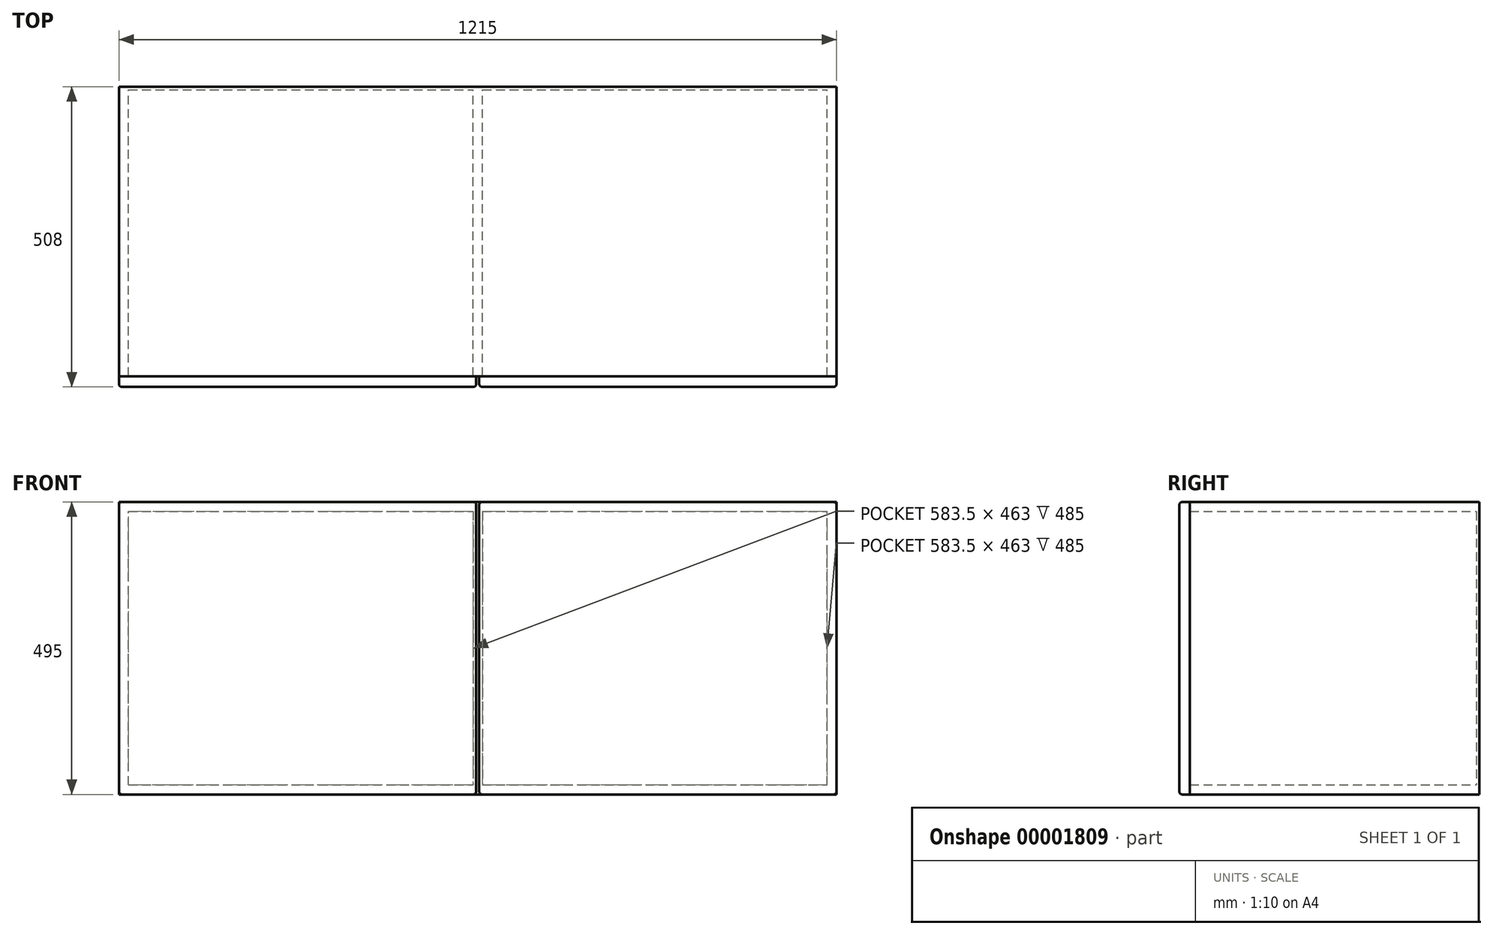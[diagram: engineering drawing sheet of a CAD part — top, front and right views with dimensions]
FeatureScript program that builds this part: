
annotation { "Feature Type Name" : "Feature", "Feature Type Description" : "" }
export const myFeature = defineFeature(function(context is Context, id is Id, definition is map)
    precondition{}
    {
        {
            var Q0;
            Q0=qCreatedBy(makeId("Front.planeOp"),FACE);
            var sketch = newSketch(context, id + "F0", { "sketchPlane" : qUnion([Q0])});
            skLineSegment(sketch, "E0.bottom", {"start": v(0, 0) * mm, "end": v(1215, 0) * mm});
            skLineSegment(sketch, "E0.top", {"start": v(0, 495) * mm, "end": v(1215, 495) * mm});
            skLineSegment(sketch, "E0.left", {"start": v(0, 0) * mm, "end": v(0, 495) * mm});
            skLineSegment(sketch, "E0.right", {"start": v(1215, 0) * mm, "end": v(1215, 495) * mm});
            skLineSegment(sketch, "E1.0", {"start": v(16, 16) * mm, "end": v(16, 479) * mm});
            skLineSegment(sketch, "E1.1", {"start": v(16, 16) * mm, "end": v(1199, 16) * mm});
            skLineSegment(sketch, "E1.2", {"start": v(1199, 16) * mm, "end": v(1199, 479) * mm});
            skLineSegment(sketch, "E1.3", {"start": v(16, 479) * mm, "end": v(1199, 479) * mm});
            skLineSegment(sketch, "E2", {"start": v(607.5, 479) * mm, "end": v(607.5, 16) * mm, "construction": true});
            skLineSegment(sketch, "E3.0", {"start": v(599.5, 479) * mm, "end": v(599.5, 16) * mm});
            skLineSegment(sketch, "E4.0", {"start": v(615.5, 479) * mm, "end": v(615.5, 16) * mm});
            skSolve(sketch);
        }
        {
            var Q0;
            Q0=makeQuery(id+"F0.imprint","IMPRINT",FACE,{"disambiguationData":[TD([[makeQuery(id+"F0.imprint","IMPRINT",EDGE,{"derivedFrom":sQuery(id+"F0.wireOp",EDGE,"E0.bottom")}),1.0]])]});
            var Q1;
            {var subQ1=sQuery(id+"F0.wireOp",EDGE,"E3.0");Q1=makeQuery(id+"F0.imprint","IMPRINT",FACE,{"disambiguationData":[TD([[makeQuery(id+"F0.imprint","IMPRINT",EDGE,{"derivedFrom":subQ1}),1.0]])]});}
            extrude(context, id + "F1", {"entities" : qUnion([Q0, Q1]), "depth" : 490 * mm});
        }
        {
            var Q0;
            {var subQ2=sQuery(id+"F0.wireOp",EDGE,"E1.0");Q0=makeQuery(id+"F0.imprint","IMPRINT",FACE,{"disambiguationData":[TD([[makeQuery(id+"F0.imprint","IMPRINT",EDGE,{"derivedFrom":subQ2}),-1.0]])]});}
            var Q1;
            {var subQ2=sQuery(id+"F0.wireOp",EDGE,"E1.2");Q1=makeQuery(id+"F0.imprint","IMPRINT",FACE,{"disambiguationData":[TD([[makeQuery(id+"F0.imprint","IMPRINT",EDGE,{"derivedFrom":subQ2}),1.0]])]});}
            extrude(context, id + "F2", {"entities" : qUnion([Q0, Q1]), "operationType" : NewBodyOperationType.ADD, "depth" : 5 * mm});
        }
        {
            var Q0;
            Q0=makeQuery(id+"F1.opExtrude","CAP_FACE",FACE,{"disambiguationData":[OSD([sQuery(id+"F0.wireOp",EDGE,"E0.bottom"),sQuery(id+"F0.wireOp",EDGE,"E0.top"),sQuery(id+"F0.wireOp",EDGE,"E0.left"),sQuery(id+"F0.wireOp",EDGE,"E0.right"),sQuery(id+"F0.wireOp",EDGE,"E1.0"),sQuery(id+"F0.wireOp",EDGE,"E1.1"),sQuery(id+"F0.wireOp",EDGE,"E1.2"),sQuery(id+"F0.wireOp",EDGE,"E1.3"),sQuery(id+"F0.wireOp",EDGE,"E3.0"),sQuery(id+"F0.wireOp",EDGE,"E4.0")])],"isStart":false});
            var sketch = newSketch(context, id + "F3", { "sketchPlane" : qUnion([Q0])});
            skLineSegment(sketch, "E5.bottom", {"start": v(0, 495) * mm, "end": v(605, 495) * mm});
            skLineSegment(sketch, "E5.top", {"start": v(0, 0) * mm, "end": v(605, 0) * mm});
            skLineSegment(sketch, "E5.left", {"start": v(0, 495) * mm, "end": v(0, 0) * mm});
            skLineSegment(sketch, "E5.right", {"start": v(605, 495) * mm, "end": v(605, 0) * mm});
            skLineSegment(sketch, "E6.bottom", {"start": v(1215, 495) * mm, "end": v(610, 495) * mm});
            skLineSegment(sketch, "E6.top", {"start": v(1215, 0) * mm, "end": v(610, 0) * mm});
            skLineSegment(sketch, "E6.left", {"start": v(1215, 495) * mm, "end": v(1215, 0) * mm});
            skLineSegment(sketch, "E6.right", {"start": v(610, 495) * mm, "end": v(610, 0) * mm});
            skSolve(sketch);
        }
        {
            var Q0;
            Q0=makeQuery(id+"F3.imprint","IMPRINT",FACE,{"disambiguationData":[TD([[makeQuery(id+"F3.imprint","IMPRINT",EDGE,{"derivedFrom":sQuery(id+"F3.wireOp",EDGE,"E5.bottom")}),-1.0]])]});
            var Q1;
            {var subQ2=sQuery(id+"F0.wireOp",EDGE,"E1.0");Q1=makeQuery(id+"F3.imprint","IMPRINT",FACE,{"disambiguationData":[TD([[makeQuery(id+"F3.imprint","IMPRINT",EDGE,{"derivedFrom":makeQuery(id+"F1.opExtrude","CAP_EDGE",EDGE,{"disambiguationData":[OSD([subQ2])],"isStart":false})}),-1.0]])]});}
            var Q2;
            Q2=makeQuery(id+"F3.imprint","IMPRINT",FACE,{"disambiguationData":[TD([[makeQuery(id+"F3.imprint","IMPRINT",EDGE,{"derivedFrom":sQuery(id+"F3.wireOp",EDGE,"E6.bottom")}),-1.0]])]});
            var Q3;
            {var subQ2=sQuery(id+"F0.wireOp",EDGE,"E1.2");Q3=makeQuery(id+"F3.imprint","IMPRINT",FACE,{"disambiguationData":[TD([[makeQuery(id+"F3.imprint","IMPRINT",EDGE,{"derivedFrom":makeQuery(id+"F1.opExtrude","CAP_EDGE",EDGE,{"disambiguationData":[OSD([subQ2])],"isStart":false})}),1.0]])]});}
            extrude(context, id + "F4", {"entities" : qUnion([Q0, Q1, Q2, Q3]), "depth" : 18 * mm});
        }
        {
            var Q0;
            Q0=makeQuery(id+"F4.opExtrude","CAP_FACE",FACE,{"disambiguationData":[OSD([sQuery(id+"F3.wireOp",EDGE,"E6.bottom"),sQuery(id+"F3.wireOp",EDGE,"E6.top"),sQuery(id+"F3.wireOp",EDGE,"E6.left"),sQuery(id+"F3.wireOp",EDGE,"E6.right")])],"isStart":false});
            var Q1;
            Q1=makeQuery(id+"F4.opExtrude","CAP_FACE",FACE,{"disambiguationData":[OSD([sQuery(id+"F3.wireOp",EDGE,"E5.bottom"),sQuery(id+"F3.wireOp",EDGE,"E5.top"),sQuery(id+"F3.wireOp",EDGE,"E5.left"),sQuery(id+"F3.wireOp",EDGE,"E5.right")])],"isStart":false});
            var Q2;
            Q2=makeQuery(id+"F4.opExtrude","SWEPT_EDGE",EDGE,{"disambiguationData":[OSD([sQuery(id+"F0.wireOp",EDGE,"E0.top"),sQuery(id+"F3.wireOp",EDGE,"E5.bottom"),sQuery(id+"F3.wireOp",EDGE,"E5.right")])]});
            var Q3;
            Q3=makeQuery(id+"F4.opExtrude","SWEPT_EDGE",EDGE,{"disambiguationData":[OSD([sQuery(id+"F0.wireOp",EDGE,"E0.top"),sQuery(id+"F3.wireOp",EDGE,"E6.bottom"),sQuery(id+"F3.wireOp",EDGE,"E6.right")])]});
            var Q4;
            Q4=makeQuery(id+"F4.opExtrude","SWEPT_EDGE",EDGE,{"disambiguationData":[OSD([sQuery(id+"F3.wireOp",EDGE,"E6.bottom"),sQuery(id+"F3.wireOp",EDGE,"E6.left")])]});
            var Q5;
            Q5=makeQuery(id+"F4.opExtrude","SWEPT_EDGE",EDGE,{"disambiguationData":[OSD([sQuery(id+"F3.wireOp",EDGE,"E6.top"),sQuery(id+"F3.wireOp",EDGE,"E6.left")])]});
            var Q6;
            Q6=makeQuery(id+"F4.opExtrude","SWEPT_EDGE",EDGE,{"disambiguationData":[OSD([sQuery(id+"F0.wireOp",EDGE,"E0.bottom"),sQuery(id+"F3.wireOp",EDGE,"E5.top"),sQuery(id+"F3.wireOp",EDGE,"E5.right")])]});
            var Q7;
            Q7=makeQuery(id+"F4.opExtrude","SWEPT_EDGE",EDGE,{"disambiguationData":[OSD([sQuery(id+"F3.wireOp",EDGE,"E5.top"),sQuery(id+"F3.wireOp",EDGE,"E5.left")])]});
            var Q8;
            Q8=makeQuery(id+"F4.opExtrude","SWEPT_EDGE",EDGE,{"disambiguationData":[OSD([sQuery(id+"F0.wireOp",EDGE,"E0.bottom"),sQuery(id+"F3.wireOp",EDGE,"E6.top"),sQuery(id+"F3.wireOp",EDGE,"E6.right")])]});
            var Q9;
            Q9=makeQuery(id+"F4.opExtrude","SWEPT_EDGE",EDGE,{"disambiguationData":[OSD([sQuery(id+"F3.wireOp",EDGE,"E5.bottom"),sQuery(id+"F3.wireOp",EDGE,"E5.left")])]});
            fillet(context, id + "F5", {"entities" : qUnion([Q0, Q1, Q2, Q3, Q4, Q5, Q6, Q7, Q8, Q9]), "radius" : 5 * mm, "tangentPropagation" : true, "allowEdgeOverflow" : false});
        }
    });
